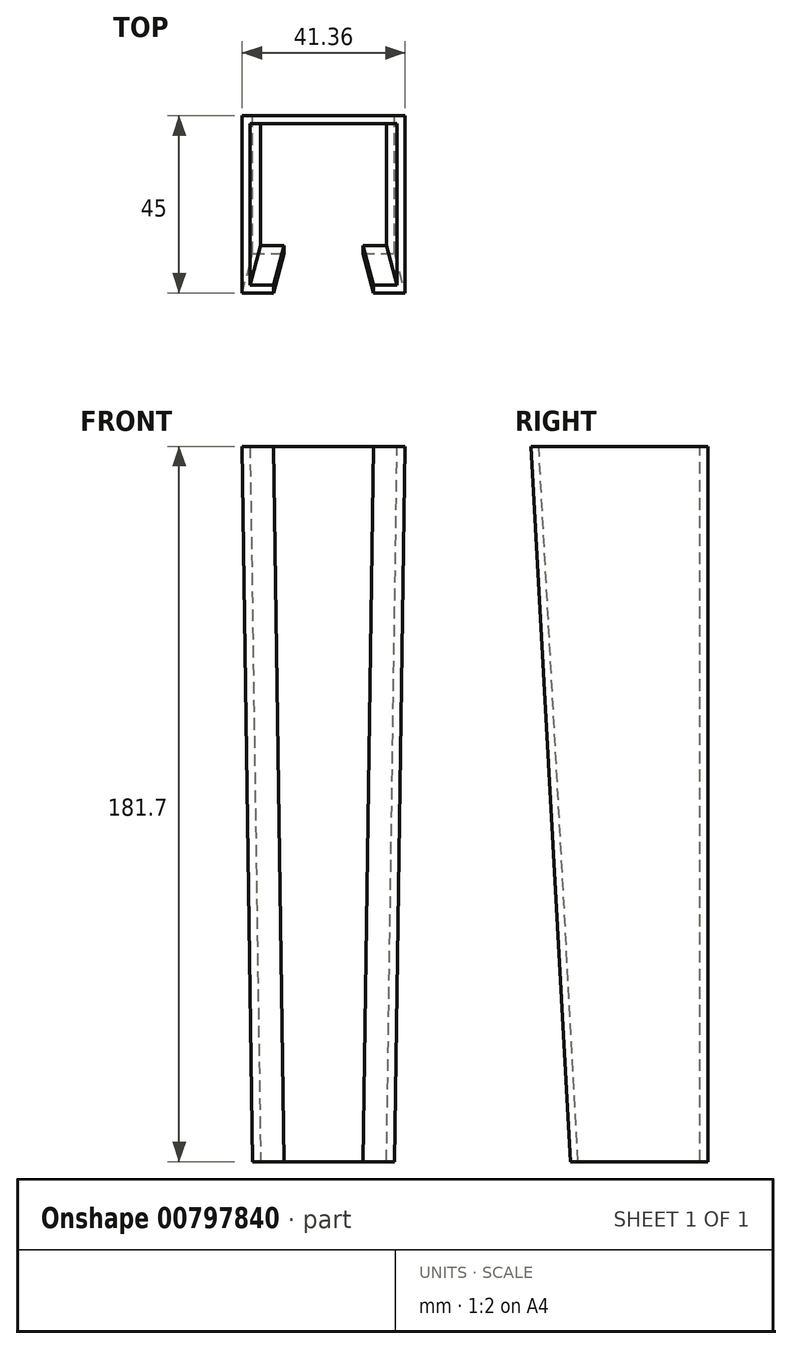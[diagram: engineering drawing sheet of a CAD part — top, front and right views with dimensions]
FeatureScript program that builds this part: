
annotation { "Feature Type Name" : "Feature", "Feature Type Description" : "" }
export const myFeature = defineFeature(function(context is Context, id is Id, definition is map)
    precondition{}
    {
        {
            var Q0;
            Q0=qCreatedBy(makeId("Front.planeOp"),FACE);
            var sketch = newSketch(context, id + "F0", { "sketchPlane" : qUnion([Q0])});
            skLineSegment(sketch, "E0", {"start": v(-18, 0) * mm, "end": v(18, 0) * mm});
            skLineSegment(sketch, "E1", {"start": v(-20.68, 181.7) * mm, "end": v(20.68, 181.7) * mm});
            skLineSegment(sketch, "E2", {"start": v(0, 147.3) * mm, "end": v(0, 0) * mm});
            skLineSegment(sketch, "E3", {"start": v(-20.17, 147.3) * mm, "end": v(20.17, 147.3) * mm});
            skLineSegment(sketch, "E4", {"start": v(-20.17, 147.3) * mm, "end": v(-18, 0) * mm});
            skLineSegment(sketch, "E5", {"start": v(18, 0) * mm, "end": v(20.17, 147.3) * mm});
            skLineSegment(sketch, "E6", {"start": v(0, 147.3) * mm, "end": v(0, 181.7) * mm});
            skLineSegment(sketch, "E7", {"start": v(-20.17, 147.3) * mm, "end": v(-20.68, 181.7) * mm});
            skLineSegment(sketch, "E8", {"start": v(20.68, 181.7) * mm, "end": v(20.18, 147.3) * mm});
            skSolve(sketch);
        }
        {
            var Q0;
            {var subQ2=sQuery(id+"F0.wireOp",EDGE,"E2");Q0=makeQuery(id+"F0.imprint","IMPRINT",FACE,{"disambiguationData":[TD([[makeQuery(id+"F0.imprint","IMPRINT",EDGE,{"derivedFrom":subQ2}),-1.0]])]});}
            var Q1;
            {var subQ2=sQuery(id+"F0.wireOp",EDGE,"E2");Q1=makeQuery(id+"F0.imprint","IMPRINT",FACE,{"disambiguationData":[TD([[makeQuery(id+"F0.imprint","IMPRINT",EDGE,{"derivedFrom":subQ2}),1.0]])]});}
            var Q2;
            {var subQ2=sQuery(id+"F0.wireOp",EDGE,"E6");Q2=makeQuery(id+"F0.imprint","IMPRINT",FACE,{"disambiguationData":[TD([[makeQuery(id+"F0.imprint","IMPRINT",EDGE,{"derivedFrom":subQ2}),-1.0]])]});}
            var Q3;
            {var subQ2=sQuery(id+"F0.wireOp",EDGE,"E6");Q3=makeQuery(id+"F0.imprint","IMPRINT",FACE,{"disambiguationData":[TD([[makeQuery(id+"F0.imprint","IMPRINT",EDGE,{"derivedFrom":subQ2}),1.0]])]});}
            extrude(context, id + "F1", {"entities" : qUnion([Q0, Q1, Q2, Q3]), "depth" : 50 * mm, "offsetDistance" : 25 * mm});
        }
        {
            var Q0;
            Q0=qCreatedBy(makeId("Right.planeOp"),FACE);
            var sketch = newSketch(context, id + "F2", { "sketchPlane" : qUnion([Q0])});
            skLineSegment(sketch, "E9.0", {"start": v(-50, 181.7) * mm, "end": v(0, 181.7) * mm});
            skLineSegment(sketch, "E10.0", {"start": v(-50, 0) * mm, "end": v(0, 0) * mm});
            skLineSegment(sketch, "E11", {"start": v(-45, 181.7) * mm, "end": v(-35, 0) * mm});
            skLineSegment(sketch, "E12.0", {"start": v(0, 181.7) * mm, "end": v(0, 0) * mm});
            skLineSegment(sketch, "E13.0", {"start": v(-50, 181.7) * mm, "end": v(-50, 0) * mm});
            skSolve(sketch);
        }
        {
            var Q0;
            {var subQ2=sQuery(id+"F2.wireOp",EDGE,"E11");Q0=makeQuery(id+"F2.imprint","IMPRINT",FACE,{"disambiguationData":[TD([[makeQuery(id+"F2.imprint","IMPRINT",EDGE,{"derivedFrom":subQ2}),-1.0]])]});}
            extrude(context, id + "F3", {"entities" : qUnion([Q0]), "operationType" : NewBodyOperationType.REMOVE, "endBound" : BoundingType.THROUGH_ALL, "oppositeDirection" : true, "depth" : 25 * mm, "offsetDistance" : 25 * mm, "hasSecondDirection" : true, "secondDirectionBound" : SecondDirectionBoundingType.THROUGH_ALL, "secondDirectionOppositeDirection" : false, "secondDirectionDepth" : 25 * mm});
        }
        {
            var Q0;
            Q0=makeQuery(id+"F1.opExtrude","SWEPT_FACE",FACE,{"disambiguationData":[OSD([sQuery(id+"F0.wireOp",EDGE,"E1")])]});
            var Q1;
            Q1=makeQuery(id+"F1.opExtrude","SWEPT_FACE",FACE,{"disambiguationData":[OSD([sQuery(id+"F0.wireOp",EDGE,"E0")])]});
            shell(context, id + "F4", {"entities" : qUnion([Q0, Q1]), "thickness" : 2 * mm});
        }
        {
            var Q0;
            Q0=makeQuery(id+"F3.boolean.opBoolean","COPY",FACE,{"derivedFrom":makeQuery(id+"F3.opExtrude","SWEPT_FACE",FACE,{"disambiguationData":[OSD([sQuery(id+"F2.wireOp",EDGE,"E11")])]})});
            var sketch = newSketch(context, id + "F5", { "sketchPlane" : qUnion([Q0])});
            skLineSegment(sketch, "E14", {"start": v(-12.68, 183.9) * mm, "end": v(-10, 1.92) * mm});
            skLineSegment(sketch, "E15", {"start": v(-10, 1.92) * mm, "end": v(10, 1.92) * mm});
            skLineSegment(sketch, "E16", {"start": v(10, 1.92) * mm, "end": v(12.68, 183.9) * mm});
            skLineSegment(sketch, "E17", {"start": v(12.68, 183.9) * mm, "end": v(-12.68, 183.9) * mm});
            skLineSegment(sketch, "E18", {"start": v(-10, 1.92) * mm, "end": v(-9.92, -3.72) * mm});
            skLineSegment(sketch, "E19", {"start": v(-9.92, -3.72) * mm, "end": v(9.92, -3.72) * mm});
            skLineSegment(sketch, "E20", {"start": v(9.92, -3.72) * mm, "end": v(10, 1.92) * mm});
            skSolve(sketch);
        }
        {
            var Q0;
            Q0 = qSketchRegion(id + "F5", true);
            extrude(context, id + "F6", {"entities" : qUnion([Q0]), "operationType" : NewBodyOperationType.REMOVE, "oppositeDirection" : true, "depth" : 25 * mm, "offsetDistance" : 25 * mm});
        }
    });
